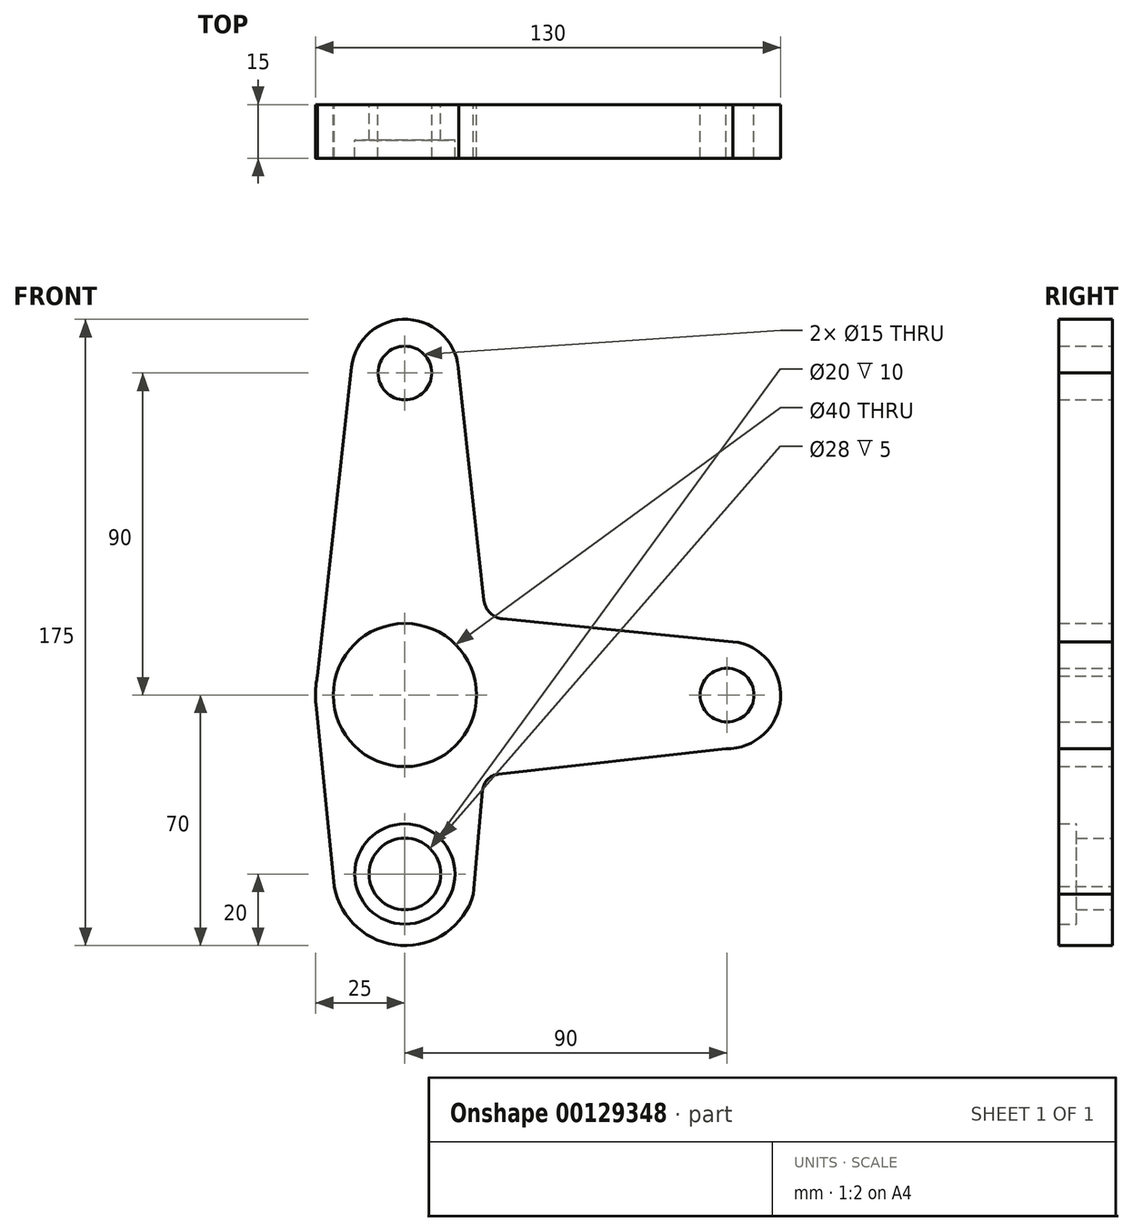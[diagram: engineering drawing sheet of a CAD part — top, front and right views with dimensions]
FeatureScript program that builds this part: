
annotation { "Feature Type Name" : "Feature", "Feature Type Description" : "" }
export const myFeature = defineFeature(function(context is Context, id is Id, definition is map)
    precondition{}
    {
        {
            var Q0;
            Q0=qCreatedBy(makeId("Front.planeOp"),FACE);
            var sketch = newSketch(context, id + "F0", { "sketchPlane" : qUnion([Q0])});
            skArc(sketch, "E0", {"start": v(-20, -0.6) * mm, "mid": v(1.44, -19.95) * mm, "end": v(19.87, 2.27) * mm});
            skCircle(sketch, "E1", {"center": v(0, 0) * mm, "radius": 10 * mm});
            skLineSegment(sketch, "E2", {"start": v(0, 0) * mm, "end": v(0, 50) * mm});
            skLineSegment(sketch, "E3", {"start": v(0, 50) * mm, "end": v(90, 50) * mm});
            skArc(sketch, "E4", {"start": v(89.67, 35) * mm, "mid": v(104.97, 49) * mm, "end": v(91.66, 64.9) * mm});
            skLineSegment(sketch, "E5", {"start": v(89.67, 35) * mm, "end": v(26.14, 27.9) * mm});
            skLineSegment(sketch, "E6", {"start": v(21.72, 23.36) * mm, "end": v(19.17, -5.69) * mm});
            skLineSegment(sketch, "E7", {"start": v(-19.7, -3.43) * mm, "end": v(-24.87, 47.47) * mm});
            skCircle(sketch, "E8", {"center": v(0, 50) * mm, "radius": 20 * mm});
            skCircle(sketch, "E9", {"center": v(90, 50) * mm, "radius": 7.5 * mm});
            skPoint(sketch, "E10.visualSharp", {"position": v(22.07, 27.44) * mm});
            skArc(sketch, "E10.filletArc", {"start": v(26.14, 27.9) * mm, "mid": v(23.12, 26.42) * mm, "end": v(21.72, 23.36) * mm});
            skLineSegment(sketch, "E11", {"start": v(0, 50) * mm, "end": v(0, 140) * mm});
            skLineSegment(sketch, "E12", {"start": v(0, 140) * mm, "end": v(42.7, 140) * mm});
            skArc(sketch, "E13", {"start": v(15, 140) * mm, "mid": v(0.82, 154.98) * mm, "end": v(-14.9, 141.64) * mm});
            skCircle(sketch, "E14", {"center": v(0, 140) * mm, "radius": 7.5 * mm});
            skLineSegment(sketch, "E15", {"start": v(-24.43, 55.31) * mm, "end": v(-14.9, 141.64) * mm});
            skLineSegment(sketch, "E16", {"start": v(22.04, 76.6) * mm, "end": v(14.91, 141.64) * mm});
            skLineSegment(sketch, "E17.trimOffspring", {"start": v(27.42, 71.28) * mm, "end": v(91.66, 64.9) * mm});
            skArc(sketch, "E18.trimOffspring", {"start": v(-24.43, 55.31) * mm, "mid": v(-24.96, 51.41) * mm, "end": v(-24.87, 47.47) * mm});
            skPoint(sketch, "E19.visualSharp", {"position": v(22.57, 71.77) * mm});
            skArc(sketch, "E19.filletArc", {"start": v(22.04, 76.6) * mm, "mid": v(23.79, 73) * mm, "end": v(27.42, 71.28) * mm});
            skSolve(sketch);
        }
        {
            var Q0;
            Q0=makeQuery(id+"F0.imprint","IMPRINT",FACE,{"disambiguationData":[TD([[makeQuery(id+"F0.imprint","IMPRINT",EDGE,{"derivedFrom":sQuery(id+"F0.wireOp",EDGE,"E1")}),-1.0]])]});
            extrude(context, id + "F1", {"entities" : qUnion([Q0]), "depth" : 15 * mm});
        }
        {
            var Q0;
            Q0=qCreatedBy(makeId("Front.planeOp"),FACE);
            var sketch = newSketch(context, id + "F2", { "sketchPlane" : qUnion([Q0])});
            skCircle(sketch, "E20", {"center": v(0, 0) * mm, "radius": 14 * mm});
            skSolve(sketch);
        }
        {
            var Q0;
            Q0 = qSketchRegion(id + "F2", true);
            extrude(context, id + "F3", {"entities" : qUnion([Q0]), "operationType" : NewBodyOperationType.REMOVE, "depth" : 25 * mm, "hasSecondDirection" : true, "secondDirectionOppositeDirection" : false, "secondDirectionDepth" : 10 * mm});
        }
    });
